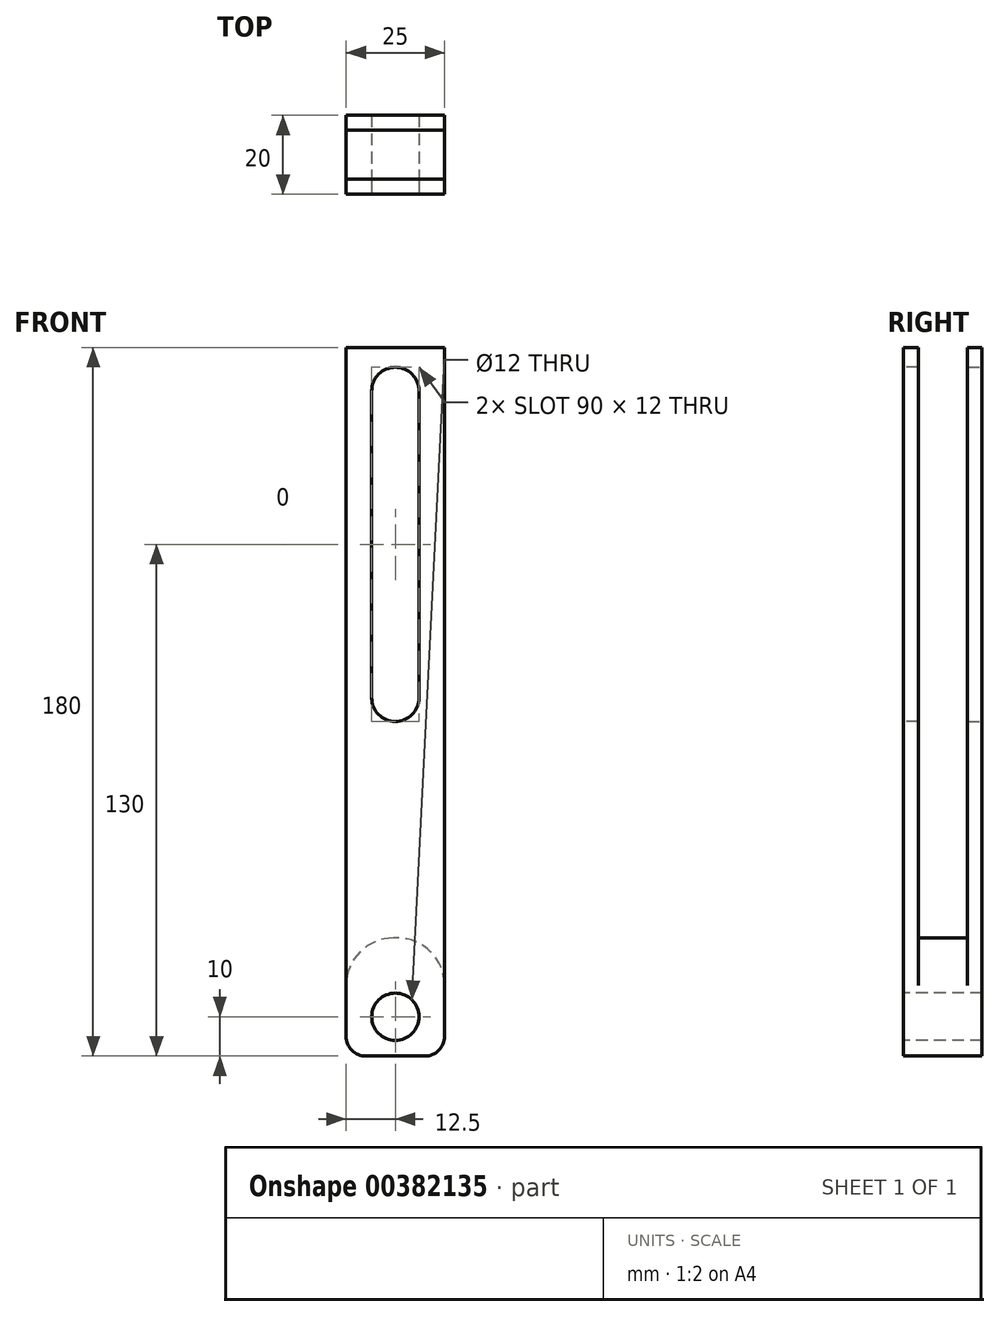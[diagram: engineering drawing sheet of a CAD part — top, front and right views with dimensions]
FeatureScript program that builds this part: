
annotation { "Feature Type Name" : "Feature", "Feature Type Description" : "" }
export const myFeature = defineFeature(function(context is Context, id is Id, definition is map)
    precondition{}
    {
        {
            var Q0;
            Q0=qCreatedBy(makeId("Right.planeOp"),FACE);
            var sketch = newSketch(context, id + "F0", { "sketchPlane" : qUnion([Q0])});
            skLineSegment(sketch, "E0.bottom", {"start": v(-10, 170) * mm, "end": v(-6.25, 170) * mm});
            skLineSegment(sketch, "E0.top", {"start": v(-10, -10) * mm, "end": v(10, -10) * mm});
            skLineSegment(sketch, "E0.left", {"start": v(-10, 170) * mm, "end": v(-10, -10) * mm});
            skLineSegment(sketch, "E0.right", {"start": v(10, 170) * mm, "end": v(10, -10) * mm});
            skLineSegment(sketch, "E1.top", {"start": v(-6.25, 20) * mm, "end": v(6.25, 20) * mm});
            skLineSegment(sketch, "E1.left", {"start": v(-6.25, 170) * mm, "end": v(-6.25, 20) * mm});
            skLineSegment(sketch, "E1.right", {"start": v(6.25, 170) * mm, "end": v(6.25, 20) * mm});
            skLineSegment(sketch, "E2.trimOffspring", {"start": v(6.25, 170) * mm, "end": v(10, 170) * mm});
            skSolve(sketch);
        }
        {
            var Q0;
            Q0=makeQuery(id+"F0.imprint","IMPRINT",FACE,{"disambiguationData":[TD([[makeQuery(id+"F0.imprint","IMPRINT",EDGE,{"derivedFrom":sQuery(id+"F0.wireOp",EDGE,"E0.bottom")}),-1.0]])]});
            extrude(context, id + "F1", {"entities" : qUnion([Q0]), "depth" : 25 * mm, "symmetric" : true});
        }
        {
            var Q0;
            Q0=makeQuery(id+"F1.opExtrude","SWEPT_FACE",FACE,{"disambiguationData":[OSD([sQuery(id+"F0.wireOp",EDGE,"E0.left")])]});
            var sketch = newSketch(context, id + "F2", { "sketchPlane" : qUnion([Q0])});
            skCircle(sketch, "E3", {"center": v(0, 0) * mm, "radius": 6 * mm});
            skSolve(sketch);
        }
        {
            var Q0;
            Q0 = qSketchRegion(id + "F2", true);
            extrude(context, id + "F3", {"entities" : qUnion([Q0]), "operationType" : NewBodyOperationType.REMOVE, "endBound" : BoundingType.THROUGH_ALL, "oppositeDirection" : true, "depth" : 25 * mm});
        }
        {
            var Q0;
            Q0=makeQuery(id+"F1.opExtrude","CAP_EDGE",EDGE,{"disambiguationData":[OSD([sQuery(id+"F0.wireOp",EDGE,"E0.top")])],"isStart":false});
            var Q1;
            Q1=makeQuery(id+"F1.opExtrude","CAP_EDGE",EDGE,{"disambiguationData":[OSD([sQuery(id+"F0.wireOp",EDGE,"E0.top")])],"isStart":true});
            fillet(context, id + "F4", {"entities" : qUnion([Q0, Q1]), "radius" : 5 * mm, "tangentPropagation" : true, "allowEdgeOverflow" : false});
        }
        {
            var Q0;
            Q0=makeQuery(id+"F1.opExtrude","CAP_EDGE",EDGE,{"disambiguationData":[OSD([sQuery(id+"F0.wireOp",EDGE,"E1.top")])],"isStart":false});
            var Q1;
            Q1=makeQuery(id+"F1.opExtrude","CAP_EDGE",EDGE,{"disambiguationData":[OSD([sQuery(id+"F0.wireOp",EDGE,"E1.top")])],"isStart":true});
            fillet(context, id + "F5", {"entities" : qUnion([Q0, Q1]), "radius" : 12 * mm, "tangentPropagation" : true, "allowEdgeOverflow" : false});
        }
        {
            var Q0;
            Q0=makeQuery(id+"F1.opExtrude","SWEPT_FACE",FACE,{"disambiguationData":[OSD([sQuery(id+"F0.wireOp",EDGE,"E0.left")])]});
            var sketch = newSketch(context, id + "F6", { "sketchPlane" : qUnion([Q0])});
            skLineSegment(sketch, "E4.bottom", {"start": v(-6, 165) * mm, "end": v(6, 165) * mm});
            skLineSegment(sketch, "E4.top", {"start": v(-6, 75) * mm, "end": v(6, 75) * mm});
            skLineSegment(sketch, "E4.left", {"start": v(-6, 165) * mm, "end": v(-6, 75) * mm});
            skLineSegment(sketch, "E4.right", {"start": v(6, 165) * mm, "end": v(6, 75) * mm});
            skSolve(sketch);
        }
        {
            var Q0;
            Q0=makeQuery(id+"F6.imprint","IMPRINT",FACE,{"disambiguationData":[TD([[makeQuery(id+"F6.imprint","IMPRINT",EDGE,{"derivedFrom":sQuery(id+"F6.wireOp",EDGE,"E4.bottom")}),-1.0]])]});
            extrude(context, id + "F7", {"entities" : qUnion([Q0]), "operationType" : NewBodyOperationType.REMOVE, "endBound" : BoundingType.THROUGH_ALL, "oppositeDirection" : true, "depth" : 25 * mm});
        }
        {
            var Q0;
            {var subQ0=sQuery(id+"F6.wireOp",EDGE,"E4.bottom");var subQ1=sQuery(id+"F6.wireOp",EDGE,"E4.left");Q0=makeQuery(id+"F7.boolean.opBoolean","COPY",EDGE,{"disambiguationData":[TD([makeQuery(id+"F1.opExtrude","SWEPT_FACE",FACE,{"disambiguationData":[OSD([sQuery(id+"F0.wireOp",EDGE,"E0.left")])]})])],"derivedFrom":makeQuery(id+"F7.opExtrude","SWEPT_EDGE",EDGE,{"disambiguationData":[OSD([subQ0,subQ1])]})});}
            var Q1;
            {var subQ0=sQuery(id+"F6.wireOp",EDGE,"E4.bottom");var subQ1=sQuery(id+"F6.wireOp",EDGE,"E4.right");Q1=makeQuery(id+"F7.boolean.opBoolean","COPY",EDGE,{"disambiguationData":[TD([makeQuery(id+"F1.opExtrude","SWEPT_FACE",FACE,{"disambiguationData":[OSD([sQuery(id+"F0.wireOp",EDGE,"E0.left")])]})])],"derivedFrom":makeQuery(id+"F7.opExtrude","SWEPT_EDGE",EDGE,{"disambiguationData":[OSD([subQ0,subQ1])]})});}
            var Q2;
            {var subQ0=sQuery(id+"F6.wireOp",EDGE,"E4.right");var subQ1=sQuery(id+"F6.wireOp",EDGE,"E4.top");Q2=makeQuery(id+"F7.boolean.opBoolean","COPY",EDGE,{"disambiguationData":[TD([makeQuery(id+"F1.opExtrude","SWEPT_FACE",FACE,{"disambiguationData":[OSD([sQuery(id+"F0.wireOp",EDGE,"E0.left")])]})])],"derivedFrom":makeQuery(id+"F7.opExtrude","SWEPT_EDGE",EDGE,{"disambiguationData":[OSD([subQ1,subQ0])]})});}
            var Q3;
            {var subQ0=sQuery(id+"F6.wireOp",EDGE,"E4.top");var subQ1=sQuery(id+"F6.wireOp",EDGE,"E4.left");Q3=makeQuery(id+"F7.boolean.opBoolean","COPY",EDGE,{"disambiguationData":[TD([makeQuery(id+"F1.opExtrude","SWEPT_FACE",FACE,{"disambiguationData":[OSD([sQuery(id+"F0.wireOp",EDGE,"E0.left")])]})])],"derivedFrom":makeQuery(id+"F7.opExtrude","SWEPT_EDGE",EDGE,{"disambiguationData":[OSD([subQ0,subQ1])]})});}
            var Q4;
            {var subQ0=sQuery(id+"F6.wireOp",EDGE,"E4.left");var subQ1=sQuery(id+"F6.wireOp",EDGE,"E4.top");Q4=makeQuery(id+"F7.boolean.opBoolean","COPY",EDGE,{"disambiguationData":[TD([makeQuery(id+"F1.opExtrude","SWEPT_FACE",FACE,{"disambiguationData":[OSD([sQuery(id+"F0.wireOp",EDGE,"E0.right")])]})])],"derivedFrom":makeQuery(id+"F7.opExtrude","SWEPT_EDGE",EDGE,{"disambiguationData":[OSD([subQ1,subQ0])]})});}
            var Q5;
            {var subQ0=sQuery(id+"F6.wireOp",EDGE,"E4.top");var subQ1=sQuery(id+"F6.wireOp",EDGE,"E4.right");Q5=makeQuery(id+"F7.boolean.opBoolean","COPY",EDGE,{"disambiguationData":[TD([makeQuery(id+"F1.opExtrude","SWEPT_FACE",FACE,{"disambiguationData":[OSD([sQuery(id+"F0.wireOp",EDGE,"E0.right")])]})])],"derivedFrom":makeQuery(id+"F7.opExtrude","SWEPT_EDGE",EDGE,{"disambiguationData":[OSD([subQ0,subQ1])]})});}
            var Q6;
            {var subQ0=sQuery(id+"F6.wireOp",EDGE,"E4.bottom");var subQ1=sQuery(id+"F6.wireOp",EDGE,"E4.right");Q6=makeQuery(id+"F7.boolean.opBoolean","COPY",EDGE,{"disambiguationData":[TD([makeQuery(id+"F1.opExtrude","SWEPT_FACE",FACE,{"disambiguationData":[OSD([sQuery(id+"F0.wireOp",EDGE,"E0.right")])]})])],"derivedFrom":makeQuery(id+"F7.opExtrude","SWEPT_EDGE",EDGE,{"disambiguationData":[OSD([subQ0,subQ1])]})});}
            var Q7;
            {var subQ0=sQuery(id+"F6.wireOp",EDGE,"E4.left");var subQ1=sQuery(id+"F6.wireOp",EDGE,"E4.bottom");Q7=makeQuery(id+"F7.boolean.opBoolean","COPY",EDGE,{"disambiguationData":[TD([makeQuery(id+"F1.opExtrude","SWEPT_FACE",FACE,{"disambiguationData":[OSD([sQuery(id+"F0.wireOp",EDGE,"E0.right")])]})])],"derivedFrom":makeQuery(id+"F7.opExtrude","SWEPT_EDGE",EDGE,{"disambiguationData":[OSD([subQ1,subQ0])]})});}
            fillet(context, id + "F8", {"entities" : qUnion([Q0, Q1, Q2, Q3, Q4, Q5, Q6, Q7]), "radius" : 6 * mm, "tangentPropagation" : true, "allowEdgeOverflow" : false});
        }
    });
